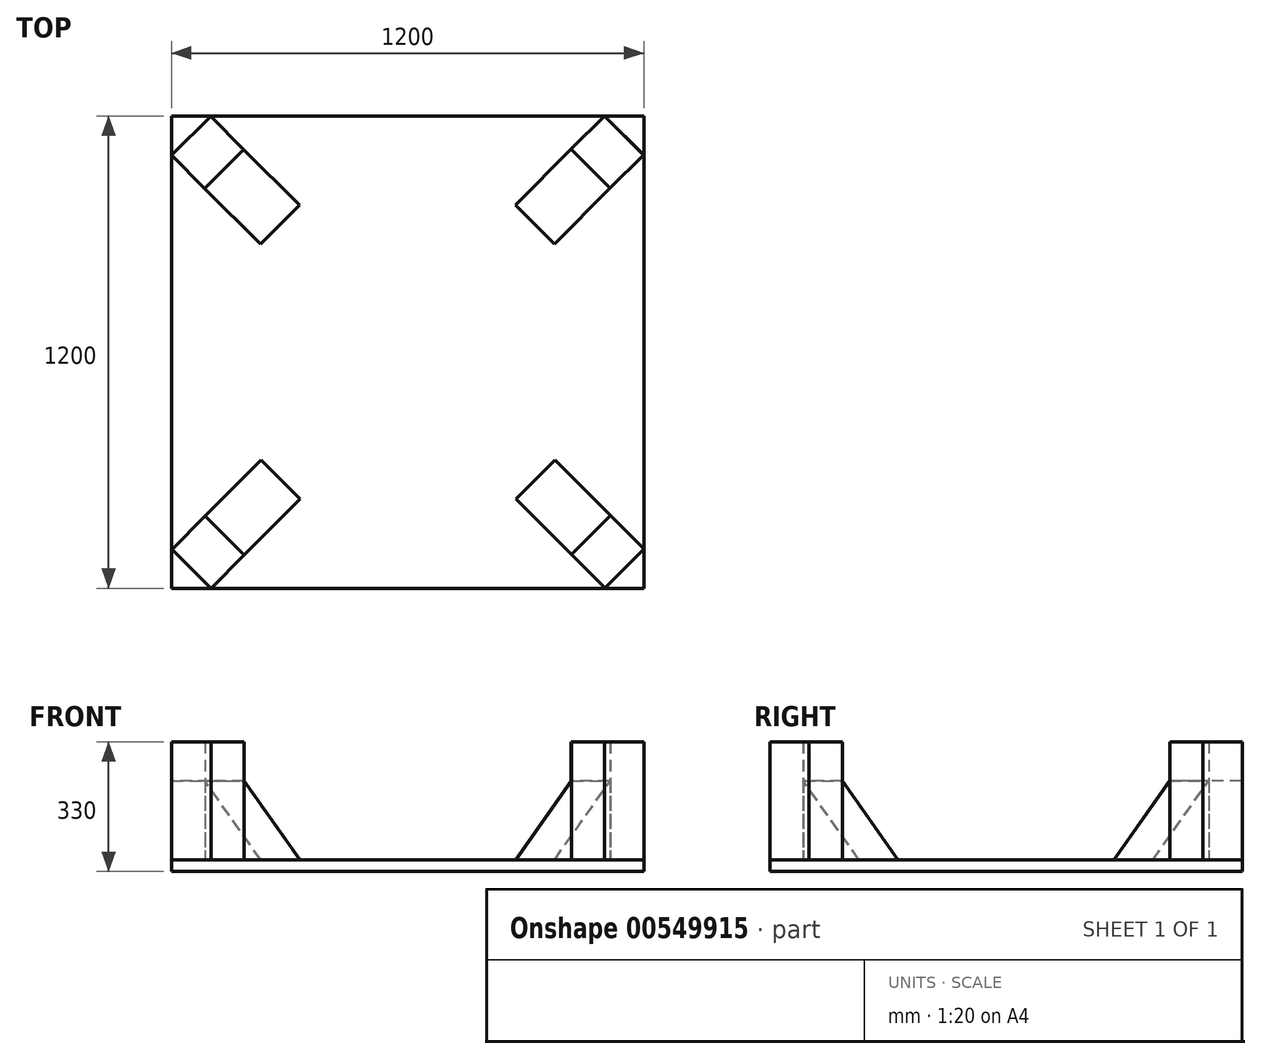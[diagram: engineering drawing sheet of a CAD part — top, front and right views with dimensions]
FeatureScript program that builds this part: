
annotation { "Feature Type Name" : "Feature", "Feature Type Description" : "" }
export const myFeature = defineFeature(function(context is Context, id is Id, definition is map)
    precondition{}
    {
        {
            var Q0;
            Q0=qCreatedBy(makeId("Top.planeOp"),FACE);
            var sketch = newSketch(context, id + "F0", { "sketchPlane" : qUnion([Q0])});
            skLineSegment(sketch, "E0", {"start": v(0, 600) * mm, "end": v(0, -600) * mm, "construction": true});
            skLineSegment(sketch, "E1", {"start": v(-600, 0) * mm, "end": v(600, 0) * mm, "construction": true});
            skLineSegment(sketch, "E2", {"start": v(-600, 600) * mm, "end": v(-600, -600) * mm});
            skLineSegment(sketch, "E3", {"start": v(-600, 600) * mm, "end": v(600, 600) * mm});
            skLineSegment(sketch, "E4", {"start": v(600, 600) * mm, "end": v(600, -600) * mm});
            skLineSegment(sketch, "E5", {"start": v(-600, -600) * mm, "end": v(600, -600) * mm});
            skSolve(sketch);
        }
        {
            var Q0;
            Q0=makeQuery(id+"F0.imprint","IMPRINT",FACE,{"disambiguationData":[TD([[makeQuery(id+"F0.imprint","IMPRINT",EDGE,{"derivedFrom":sQuery(id+"F0.wireOp",EDGE,"E2")}),1.0]])]});
            extrude(context, id + "F1", {"entities" : qUnion([Q0]), "oppositeDirection" : true, "depth" : 30 * mm, "offsetDistance" : 25 * mm});
        }
        {
            var Q0;
            Q0=makeQuery(id+"F1.opExtrude","CAP_FACE",FACE,{"disambiguationData":[OSD([sQuery(id+"F0.wireOp",EDGE,"E2"),sQuery(id+"F0.wireOp",EDGE,"E3"),sQuery(id+"F0.wireOp",EDGE,"E4"),sQuery(id+"F0.wireOp",EDGE,"E5")])],"isStart":true});
            var sketch = newSketch(context, id + "F2", { "sketchPlane" : qUnion([Q0])});
            skLineSegment(sketch, "E6", {"start": v(-600, -600) * mm, "end": v(-500, -600) * mm});
            skLineSegment(sketch, "E7", {"start": v(-500, -600) * mm, "end": v(-600, -500) * mm});
            skLineSegment(sketch, "E8", {"start": v(-600, -500) * mm, "end": v(-600, -600) * mm});
            skSolve(sketch);
        }
        {
            var Q0;
            Q0=makeQuery(id+"F2.imprint","IMPRINT",FACE,{"disambiguationData":[TD([[makeQuery(id+"F2.imprint","IMPRINT",EDGE,{"derivedFrom":sQuery(id+"F2.wireOp",EDGE,"E6")}),1.0]])]});
            extrude(context, id + "F3", {"entities" : qUnion([Q0]), "depth" : 300 * mm, "offsetDistance" : 25 * mm});
        }
        {
            var Q0;
            Q0=makeQuery(id+"F3.opExtrude","SWEPT_EDGE",EDGE,{"disambiguationData":[OSD([sQuery(id+"F0.wireOp",EDGE,"E5"),sQuery(id+"F2.wireOp",EDGE,"E6"),sQuery(id+"F2.wireOp",EDGE,"E7")])]});
            cPoint(context, id + "F4", {"entities" : qUnion([Q0]), "parameter" : 0.5});
        }
        {
            var Q0;
            Q0=qCreatedBy(id+"F4",VERTEX);
            var Q1;
            Q1=makeQuery(id+"F3.opExtrude","CAP_EDGE",EDGE,{"disambiguationData":[OSD([sQuery(id+"F2.wireOp",EDGE,"E7")])],"isStart":true});
            cPlane(context, id + "F5", {"entities" : qUnion([Q0, Q1]), "cplaneType" : CPlaneType.LINE_POINT, "offset" : 25 * mm, "width" : 150 * mm, "height" : 150 * mm});
        }
        {
            var Q0;
            Q0=qCreatedBy(id+"F5.planeOp",FACE);
            var sketch = newSketch(context, id + "F6", { "sketchPlane" : qUnion([Q0])});
            skLineSegment(sketch, "E9.0", {"start": v(777.82, 300) * mm, "end": v(777.82, 0) * mm});
            skLineSegment(sketch, "E10.0", {"start": v(848.53, 0) * mm, "end": v(0, 0) * mm});
            skLineSegment(sketch, "E11", {"start": v(777.82, 200) * mm, "end": v(577.82, 0) * mm, "construction": true});
            skLineSegment(sketch, "E12", {"start": v(458, 0) * mm, "end": v(658, 200) * mm});
            skLineSegment(sketch, "E13", {"start": v(658, 200) * mm, "end": v(658, 0) * mm});
            skLineSegment(sketch, "E14.bottom", {"start": v(658, 200) * mm, "end": v(777.82, 200) * mm, "construction": true});
            skLineSegment(sketch, "E14.top", {"start": v(658, 0) * mm, "end": v(777.82, 0) * mm});
            skLineSegment(sketch, "E14.right", {"start": v(777.82, 200) * mm, "end": v(777.82, 0) * mm});
            skLineSegment(sketch, "E15", {"start": v(777.82, 300) * mm, "end": v(658, 300) * mm});
            skLineSegment(sketch, "E16", {"start": v(658, 300) * mm, "end": v(658, 200) * mm});
            skSolve(sketch);
        }
        {
            var Q0;
            {var subQ0=sQuery(id+"F6.wireOp",EDGE,"E12");Q0=makeQuery(id+"F6.imprint","IMPRINT",FACE,{"disambiguationData":[TD([[makeQuery(id+"F6.imprint","IMPRINT",EDGE,{"derivedFrom":subQ0}),-1.0]])]});}
            var Q1;
            Q1=makeQuery(id+"F3.opExtrude","SWEPT_FACE",FACE,{"disambiguationData":[OSD([sQuery(id+"F2.wireOp",EDGE,"E8")])]});
            extrude(context, id + "F7", {"entities" : qUnion([Q0]), "depth" : 140 * mm, "endBoundEntityFace" : qUnion([Q1]), "offsetDistance" : 25 * mm});
        }
        {
            var Q0;
            Q0=qCreatedBy(makeId("Front.planeOp"),FACE);
            var sketch = newSketch(context, id + "F8", { "sketchPlane" : qUnion([Q0])});
            skLineSegment(sketch, "E17", {"start": v(0, 0) * mm, "end": v(0, 300) * mm, "construction": true});
            skSolve(sketch);
        }
        {
            var Q0;
            Q0=makeQuery(id+"F7.opExtrude","SWEPT_BODY",BODY,{"disambiguationData":[OSD([sQuery(id+"F6.wireOp",EDGE,"E9.0"),sQuery(id+"F6.wireOp",EDGE,"E10.0"),sQuery(id+"F6.wireOp",EDGE,"E11")])]});
            var Q1;
            Q1=sQuery(id+"F8.wireOp",EDGE,"E17");
            transform(context, id + "F9", {"entities" : qUnion([Q0]), "transformType" : TransformType.ROTATION, "transformAxis" : qUnion([Q1]), "angle" : 180 * degree, "makeCopy" : true});
        }
        {
            var Q0;
            Q0=makeQuery(id+"F6.imprint","IMPRINT",FACE,{"disambiguationData":[TD([[makeQuery(id+"F6.imprint","IMPRINT",EDGE,{"derivedFrom":sQuery(id+"F6.wireOp",EDGE,"E9.0")}),-1.0]])]});
            extrude(context, id + "F10", {"entities" : qUnion([Q0]), "depth" : 140 * mm, "offsetDistance" : 25 * mm});
        }
        {
            var Q0;
            Q0=makeQuery(id+"F7.opExtrude","SWEPT_BODY",BODY,{"disambiguationData":[OSD([sQuery(id+"F6.wireOp",EDGE,"E10.0"),sQuery(id+"F6.wireOp",EDGE,"E12"),sQuery(id+"F6.wireOp",EDGE,"E13")])]});
            var Q1;
            Q1=sQuery(id+"F8.wireOp",EDGE,"E17");
            transform(context, id + "F11", {"entities" : qUnion([Q0]), "transformType" : TransformType.ROTATION, "transformAxis" : qUnion([Q1]), "angle" : 90 * degree, "makeCopy" : true});
        }
        {
            var Q0;
            Q0=makeQuery(id+"F7.opExtrude","SWEPT_BODY",BODY,{"disambiguationData":[OSD([sQuery(id+"F6.wireOp",EDGE,"E10.0"),sQuery(id+"F6.wireOp",EDGE,"E12"),sQuery(id+"F6.wireOp",EDGE,"E13")])]});
            var Q1;
            Q1=sQuery(id+"F8.wireOp",EDGE,"E17");
            transform(context, id + "F12", {"entities" : qUnion([Q0]), "transformType" : TransformType.ROTATION, "transformAxis" : qUnion([Q1]), "angle" : 270 * degree, "makeCopy" : true});
        }
        {
            var Q0;
            Q0=makeQuery(id+"F10.opExtrude","SWEPT_BODY",BODY,{"disambiguationData":[OSD([sQuery(id+"F6.wireOp",EDGE,"E9.0"),sQuery(id+"F6.wireOp",EDGE,"E14.top"),sQuery(id+"F6.wireOp",EDGE,"E13"),sQuery(id+"F6.wireOp",EDGE,"E14.right"),sQuery(id+"F6.wireOp",EDGE,"E15"),sQuery(id+"F6.wireOp",EDGE,"E16")])]});
            var Q1;
            Q1=sQuery(id+"F8.wireOp",EDGE,"E17");
            transform(context, id + "F13", {"entities" : qUnion([Q0]), "transformType" : TransformType.ROTATION, "transformAxis" : qUnion([Q1]), "angle" : 90 * degree, "makeCopy" : true});
        }
        {
            var Q0;
            Q0=makeQuery(id+"F10.opExtrude","SWEPT_BODY",BODY,{"disambiguationData":[OSD([sQuery(id+"F6.wireOp",EDGE,"E9.0"),sQuery(id+"F6.wireOp",EDGE,"E14.top"),sQuery(id+"F6.wireOp",EDGE,"E13"),sQuery(id+"F6.wireOp",EDGE,"E14.right"),sQuery(id+"F6.wireOp",EDGE,"E15"),sQuery(id+"F6.wireOp",EDGE,"E16")])]});
            var Q1;
            Q1=sQuery(id+"F8.wireOp",EDGE,"E17");
            transform(context, id + "F14", {"entities" : qUnion([Q0]), "transformType" : TransformType.ROTATION, "transformAxis" : qUnion([Q1]), "angle" : 180 * degree, "makeCopy" : true});
        }
        {
            var Q0;
            Q0=makeQuery(id+"F10.opExtrude","SWEPT_BODY",BODY,{"disambiguationData":[OSD([sQuery(id+"F6.wireOp",EDGE,"E9.0"),sQuery(id+"F6.wireOp",EDGE,"E14.top"),sQuery(id+"F6.wireOp",EDGE,"E13"),sQuery(id+"F6.wireOp",EDGE,"E14.right"),sQuery(id+"F6.wireOp",EDGE,"E15"),sQuery(id+"F6.wireOp",EDGE,"E16")])]});
            var Q1;
            Q1=sQuery(id+"F8.wireOp",EDGE,"E17");
            transform(context, id + "F15", {"entities" : qUnion([Q0]), "transformType" : TransformType.ROTATION, "transformAxis" : qUnion([Q1]), "angle" : 270 * degree, "makeCopy" : true});
        }
        {
            var Q0;
            Q0=makeQuery(id+"F3.opExtrude","SWEPT_BODY",BODY,{"disambiguationData":[OSD([sQuery(id+"F2.wireOp",EDGE,"E6"),sQuery(id+"F2.wireOp",EDGE,"E7"),sQuery(id+"F2.wireOp",EDGE,"E8")])]});
            var Q1;
            Q1=sQuery(id+"F8.wireOp",EDGE,"E17");
            transform(context, id + "F16", {"entities" : qUnion([Q0]), "transformType" : TransformType.ROTATION, "transformAxis" : qUnion([Q1]), "angle" : 90 * degree, "makeCopy" : true});
        }
        {
            var Q0;
            Q0=makeQuery(id+"F3.opExtrude","SWEPT_BODY",BODY,{"disambiguationData":[OSD([sQuery(id+"F2.wireOp",EDGE,"E6"),sQuery(id+"F2.wireOp",EDGE,"E7"),sQuery(id+"F2.wireOp",EDGE,"E8")])]});
            var Q1;
            Q1=sQuery(id+"F8.wireOp",EDGE,"E17");
            transform(context, id + "F17", {"entities" : qUnion([Q0]), "transformType" : TransformType.ROTATION, "transformAxis" : qUnion([Q1]), "angle" : 180 * degree, "makeCopy" : true});
        }
        {
            var Q0;
            Q0=makeQuery(id+"F3.opExtrude","SWEPT_BODY",BODY,{"disambiguationData":[OSD([sQuery(id+"F2.wireOp",EDGE,"E6"),sQuery(id+"F2.wireOp",EDGE,"E7"),sQuery(id+"F2.wireOp",EDGE,"E8")])]});
            var Q1;
            Q1=sQuery(id+"F8.wireOp",EDGE,"E17");
            transform(context, id + "F18", {"entities" : qUnion([Q0]), "transformType" : TransformType.ROTATION, "transformAxis" : qUnion([Q1]), "angle" : 270 * degree, "makeCopy" : true});
        }
        {
            var Q0;
            Q0=makeQuery(id+"F15.opPattern","COPY",BODY,{"derivedFrom":makeQuery(id+"F10.opExtrude","SWEPT_BODY",BODY,{"disambiguationData":[OSD([sQuery(id+"F6.wireOp",EDGE,"E9.0"),sQuery(id+"F6.wireOp",EDGE,"E14.top"),sQuery(id+"F6.wireOp",EDGE,"E13"),sQuery(id+"F6.wireOp",EDGE,"E14.right"),sQuery(id+"F6.wireOp",EDGE,"E15"),sQuery(id+"F6.wireOp",EDGE,"E16")])]}),"instanceName":"1"});
            deleteBodies(context, id + "F19", {"entities" : qUnion([Q0])});
        }
        {
            var Q0;
            Q0=makeQuery(id+"F12.opPattern","COPY",FACE,{"derivedFrom":makeQuery(id+"F7.opExtrude","SWEPT_FACE",FACE,{"disambiguationData":[OSD([sQuery(id+"F6.wireOp",EDGE,"E13")])]}),"instanceName":"1"});
            extrude(context, id + "F20", {"entities" : qUnion([Q0]), "operationType" : NewBodyOperationType.ADD, "endBound" : BoundingType.UP_TO_NEXT, "depth" : 25 * mm, "offsetDistance" : 25 * mm});
        }
    });
